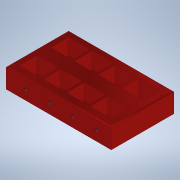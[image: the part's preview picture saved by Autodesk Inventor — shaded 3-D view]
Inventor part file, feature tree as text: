
AUTODESK INVENTOR PART (.ipt)
format: ipt  version: 2022 (Build 260153000, 153)  size: 288,256 bytes
history: native  units: mm
features: sketch x6, hole x4, projected_geometry x3, extrude x2, chamfer x1
ambient origin geometry x8: Origin, YZ Plane, XZ Plane, XY Plane, X Axis, Y Axis, Z Axis, Center Point
bodies: Volumenkörper1 (feature_tree)
feature tree (16):
  extrude  "Extrusion1"  Depth=139.7mm
  chamfer  "Fase1"  Distance=44.45mm
  sketch  "Skizze4"  dims[d11=2.0mm d12=2.0mm d13=45.0deg d153=24.0mm]
  hole  "Bohrung7"  [1 undecoded]
  extrude  "Extrusion5"  Depth=5.0mm
  hole  "Hole9"  [1 undecoded]
  hole  "Hole10"  [1 undecoded]
  hole  "Hole11"  [1 undecoded]
  sketch  "Skizze1"  dims[d0=234.95mm d2=139.7mm d3=44.45mm d4=0.0mm]
  sketch  "Sketch12"  dims[d154=24.0mm d155=5.0mm]
  projected_geometry  "Projected Loop1"
  projected_geometry  "Projected Loop2"
  projected_geometry  "Projected Loop3"
  sketch  "Sketch13"  dims[d156=5.0mm d157=24.0mm]
  sketch  "Sketch14"  dims[d158=5.0mm d159=5.0mm]
  sketch  "Sketch15"  dims[d160=24.0mm d161=24.0mm d162=5.0mm d163=5.0mm d164=24.0mm d165=5.0mm d166=24.0mm d167=5.0mm d168=24.0mm d169=3.242mm d170=6.0mm d171=8.0mm d172=4.6mm d173=14.3117mm d174=20.0mm d175=20.594885mm d193=47.75mm d194=40.0mm d195=8.5mm d196=8.5mm d197=3.0mm d198=40.0mm d200=52.75mm d201=20.0mm d203=70.0mm d206=36.0mm d207=0.0mm d209=23.0mm d210=40.0mm d212=52.75mm d213=10.0mm d215=10.0mm d217=7.95mm d218=6.924mm d219=0.624793mm d220=8.304mm d221=4.0mm d222=2.0mm d223=90.0deg d224=8.0mm d225=20.594885mm d226=40.0mm d228=52.75mm d229=10.0mm d231=10.0mm d233=7.95mm d234=6.924mm d235=0.624793mm d236=8.304mm d237=4.0mm d238=2.0mm d239=90.0deg d240=8.0mm d241=20.594885mm d242=25.0mm d243=25.0mm d244=20.0mm d246=50.0mm d247=20.0mm d249=50.0mm d252=6.756mm d253=6.924mm d254=12.878mm d255=2.0mm d256=14.3117mm d257=8.0mm d258=20.594885mm]
note: 4 required parameter values undecoded (feature->parameter linkage not recoverable at this tier; creation-order binding heuristic only, values carry confidence <= 0.55)
